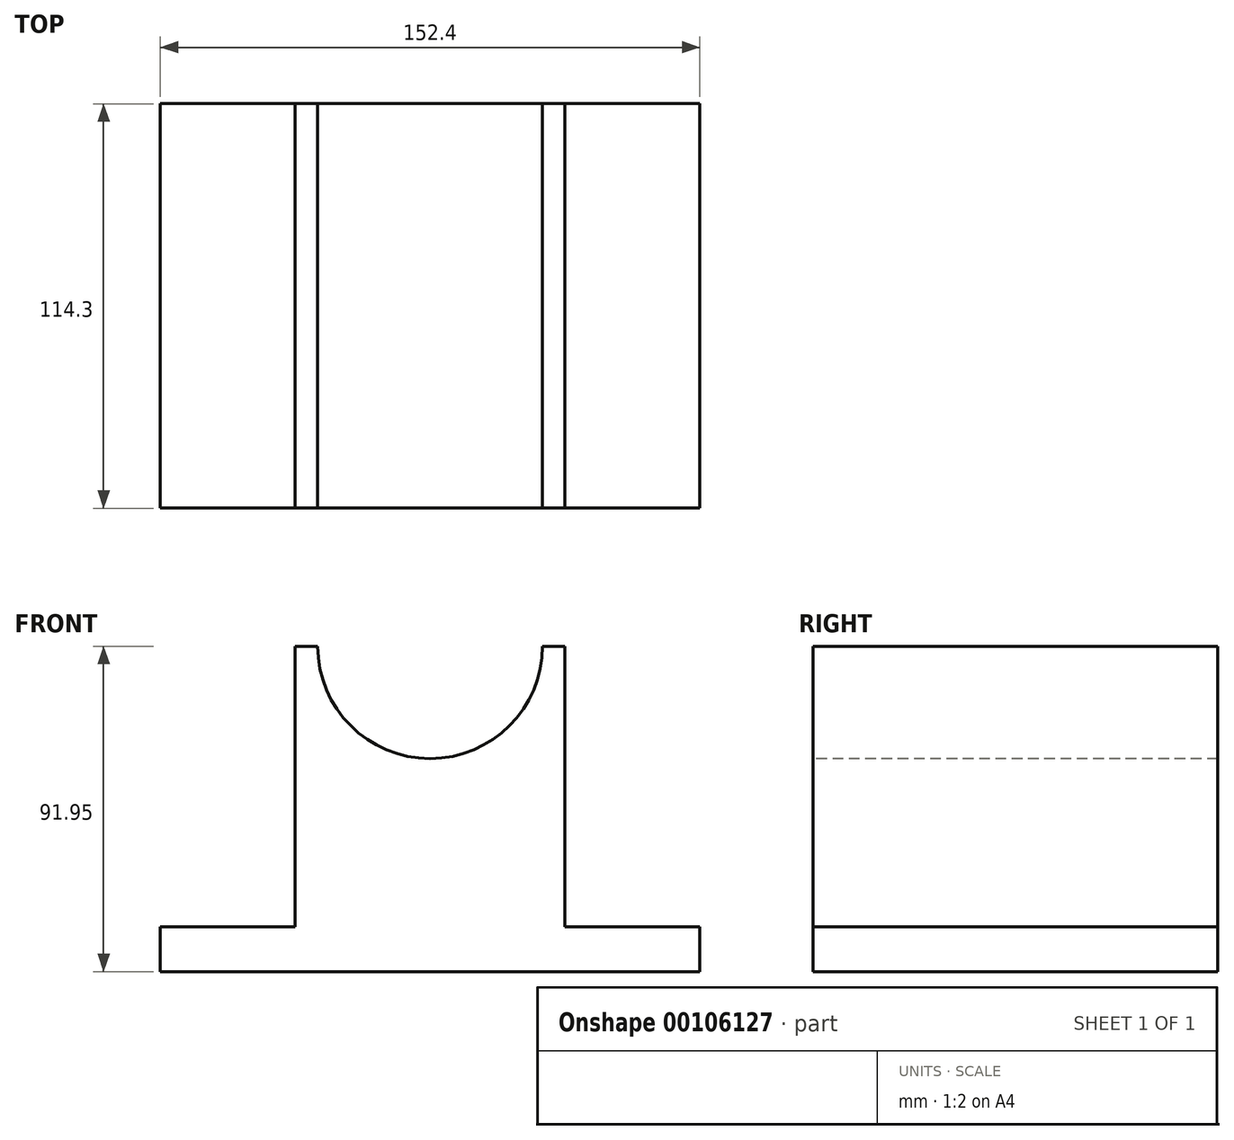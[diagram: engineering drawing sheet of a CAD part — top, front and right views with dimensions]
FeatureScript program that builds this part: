
annotation { "Feature Type Name" : "Feature", "Feature Type Description" : "" }
export const myFeature = defineFeature(function(context is Context, id is Id, definition is map)
    precondition{}
    {
        {
            var Q0;
            Q0=qCreatedBy(makeId("Top.planeOp"),FACE);
            var sketch = newSketch(context, id + "F0", { "sketchPlane" : qUnion([Q0])});
            skLineSegment(sketch, "E0.bottom", {"start": v(-51.76, 49.67) * mm, "end": v(100.64, 49.67) * mm});
            skLineSegment(sketch, "E0.top", {"start": v(-51.76, -64.63) * mm, "end": v(100.64, -64.63) * mm});
            skLineSegment(sketch, "E0.left", {"start": v(-51.76, 49.67) * mm, "end": v(-51.76, -64.63) * mm});
            skLineSegment(sketch, "E0.right", {"start": v(100.64, 49.67) * mm, "end": v(100.64, -64.63) * mm});
            skSolve(sketch);
        }
        {
            var Q0;
            Q0 = qSketchRegion(id + "F0", true);
            extrude(context, id + "F1", {"entities" : qUnion([Q0]), "depth" : 12.7 * mm});
        }
        {
            var Q0;
            Q0=makeQuery(id+"F1.opExtrude","CAP_FACE",FACE,{"disambiguationData":[OSD([sQuery(id+"F0.wireOp",EDGE,"E0.bottom"),sQuery(id+"F0.wireOp",EDGE,"E0.top"),sQuery(id+"F0.wireOp",EDGE,"E0.left"),sQuery(id+"F0.wireOp",EDGE,"E0.right")])],"isStart":false});
            var sketch = newSketch(context, id + "F2", { "sketchPlane" : qUnion([Q0])});
            skLineSegment(sketch, "E1", {"start": v(-51.76, 49.67) * mm, "end": v(-13.66, 49.67) * mm});
            skLineSegment(sketch, "E2.bottom", {"start": v(-13.66, 49.67) * mm, "end": v(62.54, 49.67) * mm});
            skLineSegment(sketch, "E2.top", {"start": v(-13.66, -64.63) * mm, "end": v(62.54, -64.63) * mm});
            skLineSegment(sketch, "E2.left", {"start": v(-13.66, 49.67) * mm, "end": v(-13.66, -64.63) * mm});
            skLineSegment(sketch, "E2.right", {"start": v(62.54, 49.67) * mm, "end": v(62.54, -64.63) * mm});
            skSolve(sketch);
        }
        {
            var Q0;
            Q0 = qSketchRegion(id + "F2", true);
            extrude(context, id + "F3", {"entities" : qUnion([Q0]), "operationType" : NewBodyOperationType.ADD, "depth" : 79.25 * mm});
        }
        {
            var Q0;
            Q0=makeQuery(id+"F3.boolean.opBoolean","MERGE",FACE,{"derivedFrom":[makeQuery(id+"F1.opExtrude","SWEPT_FACE",FACE,{"disambiguationData":[OSD([sQuery(id+"F0.wireOp",EDGE,"E0.top")])]}),makeQuery(id+"F3.opExtrude","SWEPT_FACE",FACE,{"disambiguationData":[OSD([sQuery(id+"F2.wireOp",EDGE,"E2.top")])]})]});
            var sketch = newSketch(context, id + "F4", { "sketchPlane" : qUnion([Q0])});
            skLineSegment(sketch, "E3", {"start": v(-13.66, 91.95) * mm, "end": v(24.44, 91.95) * mm});
            skLineSegment(sketch, "E4", {"start": v(24.44, 91.95) * mm, "end": v(24.44, 60.2) * mm});
            skCircle(sketch, "E5", {"center": v(24.44, 91.95) * mm, "radius": 31.75 * mm});
            skSolve(sketch);
        }
        {
            var Q0;
            {var subQ0=sQuery(id+"F4.wireOp",EDGE,"E4");Q0=makeQuery(id+"F4.imprint","IMPRINT",FACE,{"disambiguationData":[TD([[makeQuery(id+"F4.imprint","IMPRINT",EDGE,{"derivedFrom":subQ0}),1.0]])]});}
            var Q1;
            {var subQ0=sQuery(id+"F4.wireOp",EDGE,"E4");Q1=makeQuery(id+"F4.imprint","IMPRINT",FACE,{"disambiguationData":[TD([[makeQuery(id+"F4.imprint","IMPRINT",EDGE,{"derivedFrom":subQ0}),-1.0]])]});}
            extrude(context, id + "F5", {"entities" : qUnion([Q0, Q1]), "operationType" : NewBodyOperationType.REMOVE, "endBound" : BoundingType.THROUGH_ALL, "oppositeDirection" : true, "depth" : 25.4 * mm});
        }
    });
